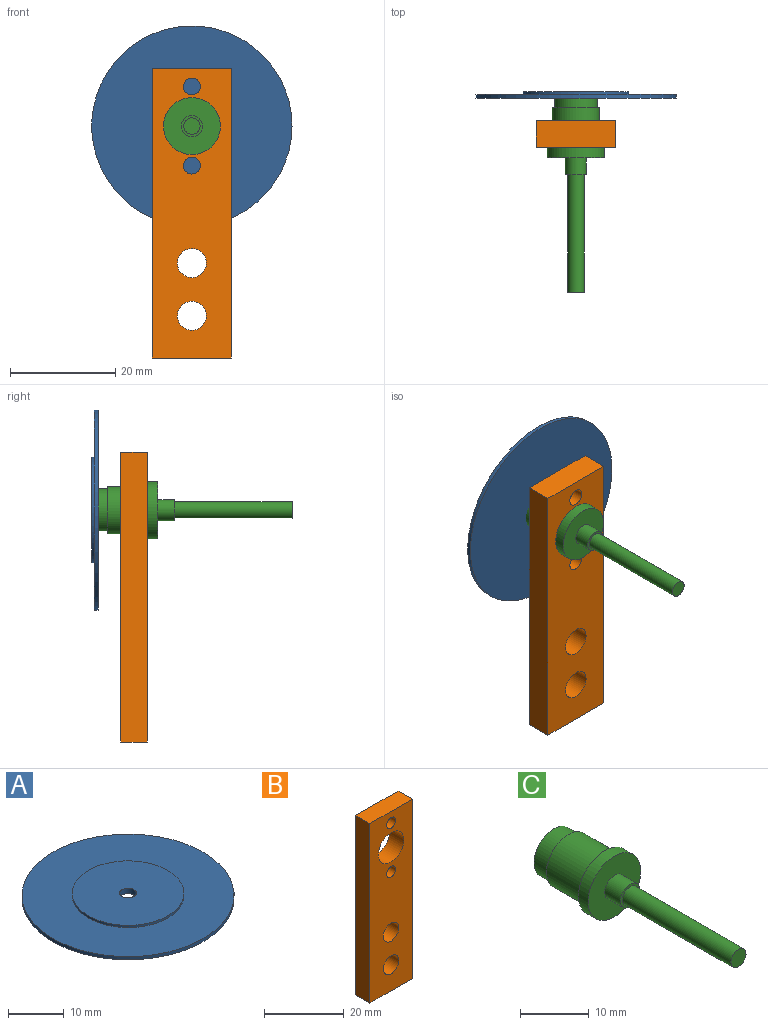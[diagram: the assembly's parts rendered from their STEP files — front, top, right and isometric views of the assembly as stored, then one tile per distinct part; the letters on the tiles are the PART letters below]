
ASSEMBLY  parts=3 mates=4
PART A: 6 faces, bbox 38x38x1.2 mm
  f0: cylinder r=19mm len=38mm, axis (0,0,-1), area 83.6mm2, adj f1,f2
  f1: plane 38x38mm, normal (0,0,1), area 820mm2, adj f0,f3
  f2: plane 38x38mm, normal (0,0,-1), area 1127mm2, adj f0,f5
  f3: cylinder r=10mm len=20mm, axis (0,0,-1), area 31.4mm2, adj f1,f4
  f4: plane 20x20mm, normal (0,0,1), area 307.1mm2, adj f3,f5
  f5: cylinder r=1.5mm len=3mm, axis (0,0,1), area 11.3mm2, adj f2,f4
PART B: 11 faces, bbox 15x5x55 mm
  f0: plane 15x5mm, normal (0,0,1), area 75mm2, adj f1,f2,f3,f4
  f1: plane 55x5mm, normal (-1,0,0), area 275mm2, adj f0,f3,f4,f8
  f2: plane 55x5mm, normal (1,0,0), area 275mm2, adj f0,f3,f4,f8
  f3: plane 55x15mm, normal (0,-1,0), area 697.8mm2, adj f0,f1,f2,f5,f6,f7,f8,f9
  f4: plane 55x15mm, normal (0,1,0), area 697.8mm2, adj f0,f1,f2,f5,f6,f7,f8,f9
  f5: cylinder r=1.6mm len=5mm, axis (0,-1,0), area 50.3mm2, adj f3,f4
  f6: cylinder r=4.5mm len=9mm, axis (0,-1,0), area 141.4mm2, adj f3,f4
  f7: cylinder r=1.6mm len=5mm, axis (0,-1,0), area 50.3mm2, adj f3,f4
  f8: plane 15x5mm, normal (0,0,-1), area 75mm2, adj f1,f2,f3,f4
  f9: cylinder r=2.75mm len=5.5mm, axis (0,-1,0), area 86.4mm2, adj f3,f4
  f10: cylinder r=2.75mm len=5.5mm, axis (0,-1,0), area 86.4mm2, adj f3,f4
PART C: 11 faces, bbox 10.8x38x10.8 mm
  f0: plane 3.1x3.1mm, normal (0,-1,0), area 7.5mm2, adj f10
  f1: plane 8.07x8.07mm, normal (0,1,0), area 51.1mm2, adj f2
  f2: cylinder r=4.04mm len=8.07mm, axis (0,1,0), area 76.1mm2, adj f1,f3
  f3: plane 8.94x8.94mm, normal (0,1,0), area 11.6mm2, adj f2,f4
  f4: cylinder r=4.47mm len=8.94mm, axis (0,1,0), area 210.6mm2, adj f3,f5
  f5: plane 10.8x10.8mm, normal (0,1,0), area 28.8mm2, adj f4,f6
  f6: cylinder r=5.4mm len=10.8mm, axis (0,1,0), area 67.9mm2, adj f5,f7
  f7: plane 10.8x10.8mm, normal (0,-1,0), area 79mm2, adj f6,f8
  f8: cylinder r=2mm len=4mm, axis (0,1,0), area 40.2mm2, adj f7,f9
  f9: plane 4x4mm, normal (0,-1,0), area 5mm2, adj f8,f10
  f10: cylinder r=1.55mm len=22.3mm, axis (0,1,0), area 217.2mm2, adj f0,f9
PLACE A rot(axis=(-1,0,0),90deg) t=(-26.47,-35.82,-26.27)mm
PLACE B t=(-26.47,-40.12,-30.27)mm
PLACE C t=(-26.47,-59.82,-26.27)mm
MATE cylindrical C.f2 <-> B.f6  axis (0,1,0) through (-26.47,-41.37,-26.27)mm
MATE cylindrical A.f5 <-> C.f2  axis (0,1,0) through (-26.47,-34.62,-26.27)mm
MATE planar A.f0 <-> C.f2  axis (0,-1,0) through (-26.47,-35.82,-26.27)mm
MATE planar C.f2 <-> B.f3  axis (0,1,0) through (-26.47,-45.12,-26.27)mm
